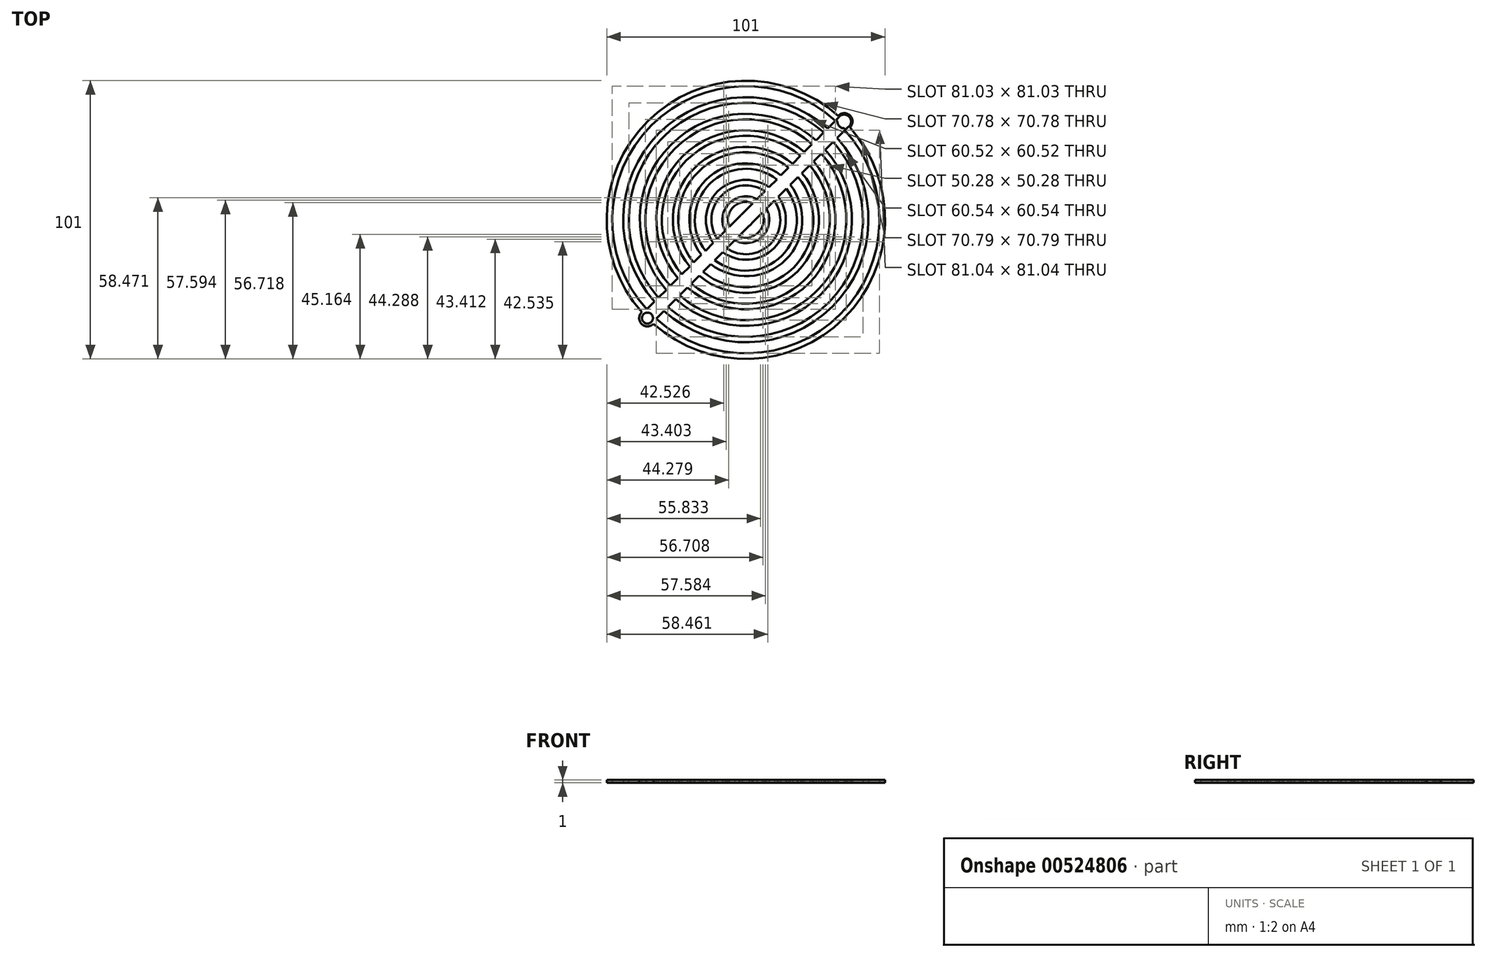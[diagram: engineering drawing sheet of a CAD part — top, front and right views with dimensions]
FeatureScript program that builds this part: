
annotation { "Feature Type Name" : "Feature", "Feature Type Description" : "" }
export const myFeature = defineFeature(function(context is Context, id is Id, definition is map)
    precondition{}
    {
        {
            var Q0;
            Q0=qCreatedBy(makeId("Top.planeOp"),FACE);
            var sketch = newSketch(context, id + "F0", { "sketchPlane" : qUnion([Q0])});
            skArc(sketch, "E0", {"start": v(-58.86, 36.16) * mm, "mid": v(-58.29, 36.6) * mm, "end": v(-57.86, 37.16) * mm});
            skArc(sketch, "E1.0", {"start": v(-57.5, 44.34) * mm, "mid": v(-64.65, 42.96) * mm, "end": v(-66.03, 35.8) * mm});
            skArc(sketch, "E2.0", {"start": v(-56, 45.83) * mm, "mid": v(-66.06, 44.37) * mm, "end": v(-67.52, 34.3) * mm});
            skArc(sketch, "E3.0", {"start": v(-53.1, 48.74) * mm, "mid": v(-68.9, 47.2) * mm, "end": v(-70.43, 31.4) * mm});
            skArc(sketch, "E4.0", {"start": v(-51.65, 50.18) * mm, "mid": v(-70.3, 48.61) * mm, "end": v(-71.87, 29.96) * mm});
            skLineSegment(sketch, "E5.bottom", {"start": v(-94.5, 72.8) * mm, "end": v(-25.6, 72.8) * mm, "construction": true});
            skLineSegment(sketch, "E5.top", {"start": v(-94.5, 3.92) * mm, "end": v(-25.6, 3.92) * mm, "construction": true});
            skLineSegment(sketch, "E5.left", {"start": v(-94.5, 72.8) * mm, "end": v(-94.5, 3.92) * mm, "construction": true});
            skLineSegment(sketch, "E5.right", {"start": v(-25.6, 72.8) * mm, "end": v(-25.6, 3.92) * mm, "construction": true});
            skArc(sketch, "E6.0", {"start": v(-48.8, 53.04) * mm, "mid": v(-73.13, 51.44) * mm, "end": v(-74.73, 27.1) * mm});
            skArc(sketch, "E7.0", {"start": v(-47.37, 54.46) * mm, "mid": v(-74.55, 52.86) * mm, "end": v(-76.16, 25.67) * mm});
            skArc(sketch, "E8.0", {"start": v(-44.52, 57.3) * mm, "mid": v(-77.38, 55.68) * mm, "end": v(-79, 22.83) * mm});
            skArc(sketch, "E9.0", {"start": v(-43.1, 58.73) * mm, "mid": v(-78.8, 57.1) * mm, "end": v(-80.42, 21.4) * mm});
            skArc(sketch, "E10.0", {"start": v(-40.26, 61.57) * mm, "mid": v(-81.62, 59.93) * mm, "end": v(-83.26, 18.57) * mm});
            skArc(sketch, "E11.0", {"start": v(-38.85, 62.99) * mm, "mid": v(-83.03, 61.34) * mm, "end": v(-84.68, 17.15) * mm});
            skArc(sketch, "E12.0", {"start": v(-36, 65.82) * mm, "mid": v(-85.86, 64.17) * mm, "end": v(-87.52, 14.32) * mm});
            skArc(sketch, "E13.0", {"start": v(-34.6, 67.24) * mm, "mid": v(-87.28, 65.58) * mm, "end": v(-88.93, 12.9) * mm});
            skArc(sketch, "E14.0", {"start": v(-31.76, 70.07) * mm, "mid": v(-90.1, 68.41) * mm, "end": v(-91.77, 10.07) * mm});
            skArc(sketch, "E15.0", {"start": v(-30.34, 71.49) * mm, "mid": v(-91.52, 69.83) * mm, "end": v(-93.18, 8.65) * mm});
            skArc(sketch, "E16.0", {"start": v(-27.51, 74.32) * mm, "mid": v(-94.35, 72.65) * mm, "end": v(-96.01, 5.82) * mm});
            skArc(sketch, "E17.0", {"start": v(-26.1, 75.74) * mm, "mid": v(-95.76, 74.07) * mm, "end": v(-97.43, 4.4) * mm});
            skLineSegment(sketch, "E18.0", {"start": v(-26.1, 75.74) * mm, "end": v(-27.3, 74.52) * mm});
            skLineSegment(sketch, "E19.0", {"start": v(-22.69, 72.33) * mm, "end": v(-23.92, 71.1) * mm});
            skLineSegment(sketch, "E20.trimOffspring", {"start": v(-48.8, 53.04) * mm, "end": v(-51.65, 50.18) * mm});
            skLineSegment(sketch, "E21.trimOffspring", {"start": v(-45.39, 49.64) * mm, "end": v(-48.25, 46.78) * mm});
            skLineSegment(sketch, "E22.trimOffspring", {"start": v(-44.52, 57.3) * mm, "end": v(-47.37, 54.46) * mm});
            skLineSegment(sketch, "E23", {"start": v(-96.22, 5.62) * mm, "end": v(-92.8, 2.23) * mm});
            skLineSegment(sketch, "E24", {"start": v(-27.3, 74.52) * mm, "end": v(-23.92, 71.1) * mm});
            skLineSegment(sketch, "E25.trimOffspring", {"start": v(-41.12, 53.9) * mm, "end": v(-43.96, 51.06) * mm});
            skLineSegment(sketch, "E26.trimOffspring", {"start": v(-36.86, 58.16) * mm, "end": v(-39.7, 55.33) * mm});
            skLineSegment(sketch, "E27.trimOffspring", {"start": v(-40.26, 61.57) * mm, "end": v(-43.1, 58.73) * mm});
            skLineSegment(sketch, "E28.trimOffspring", {"start": v(-36, 65.82) * mm, "end": v(-38.85, 62.99) * mm});
            skLineSegment(sketch, "E29.trimOffspring", {"start": v(-32.6, 62.42) * mm, "end": v(-35.44, 59.58) * mm});
            skLineSegment(sketch, "E30.trimOffspring", {"start": v(-28.35, 66.67) * mm, "end": v(-31.19, 63.83) * mm});
            skLineSegment(sketch, "E31.trimOffspring", {"start": v(-31.76, 70.07) * mm, "end": v(-34.6, 67.24) * mm});
            skLineSegment(sketch, "E32.trimOffspring", {"start": v(-27.51, 74.32) * mm, "end": v(-30.34, 71.49) * mm});
            skLineSegment(sketch, "E33.trimOffspring", {"start": v(-24.1, 70.92) * mm, "end": v(-26.94, 68.08) * mm});
            skLineSegment(sketch, "E34.trimOffspring", {"start": v(-53.1, 48.74) * mm, "end": v(-56, 45.83) * mm});
            skLineSegment(sketch, "E35.trimOffspring", {"start": v(-49.68, 45.34) * mm, "end": v(-52.6, 42.43) * mm});
            skLineSegment(sketch, "E36.trimOffspring", {"start": v(-57.5, 44.34) * mm, "end": v(-61.31, 40.52) * mm});
            skLineSegment(sketch, "E37.trimOffspring", {"start": v(-54.09, 40.94) * mm, "end": v(-57.86, 37.16) * mm});
            skArc(sketch, "E38.trimOffspring", {"start": v(-62.63, 32.4) * mm, "mid": v(-55.46, 33.76) * mm, "end": v(-54.09, 40.94) * mm});
            skLineSegment(sketch, "E39.trimOffspring", {"start": v(-62.21, 39.62) * mm, "end": v(-66.03, 35.8) * mm});
            skLineSegment(sketch, "E40.trimOffspring", {"start": v(-58.86, 36.16) * mm, "end": v(-62.63, 32.4) * mm});
            skArc(sketch, "E41.trimOffspring", {"start": v(-61.31, 40.52) * mm, "mid": v(-61.82, 40.13) * mm, "end": v(-62.21, 39.62) * mm});
            skArc(sketch, "E42.trimOffspring", {"start": v(-67.03, 27.99) * mm, "mid": v(-51.21, 29.52) * mm, "end": v(-49.68, 45.34) * mm});
            skArc(sketch, "E43.trimOffspring", {"start": v(-68.47, 26.55) * mm, "mid": v(-49.8, 28.1) * mm, "end": v(-48.25, 46.78) * mm});
            skLineSegment(sketch, "E44.trimOffspring", {"start": v(-67.52, 34.3) * mm, "end": v(-70.43, 31.4) * mm});
            skLineSegment(sketch, "E45.trimOffspring", {"start": v(-64.12, 30.9) * mm, "end": v(-67.03, 27.99) * mm});
            skLineSegment(sketch, "E46.trimOffspring", {"start": v(-68.47, 26.55) * mm, "end": v(-71.33, 23.7) * mm});
            skLineSegment(sketch, "E47.trimOffspring", {"start": v(-71.87, 29.96) * mm, "end": v(-74.73, 27.1) * mm});
            skLineSegment(sketch, "E48.trimOffspring", {"start": v(-76.16, 25.67) * mm, "end": v(-79, 22.83) * mm});
            skLineSegment(sketch, "E49.trimOffspring", {"start": v(-72.75, 22.27) * mm, "end": v(-75.6, 19.42) * mm});
            skLineSegment(sketch, "E50.trimOffspring", {"start": v(-77.02, 18) * mm, "end": v(-79.86, 15.16) * mm});
            skLineSegment(sketch, "E51.trimOffspring", {"start": v(-80.42, 21.4) * mm, "end": v(-83.26, 18.57) * mm});
            skArc(sketch, "E52.trimOffspring", {"start": v(-94.03, 1) * mm, "mid": v(-24.34, 2.65) * mm, "end": v(-22.69, 72.33) * mm});
            skLineSegment(sketch, "E53.trimOffspring", {"start": v(-96.22, 5.62) * mm, "end": v(-97.43, 4.4) * mm});
            skArc(sketch, "E54.trimOffspring", {"start": v(-92.61, 2.41) * mm, "mid": v(-25.76, 4.06) * mm, "end": v(-24.1, 70.92) * mm});
            skLineSegment(sketch, "E55.trimOffspring", {"start": v(-92.8, 2.23) * mm, "end": v(-94.03, 1) * mm});
            skArc(sketch, "E56.trimOffspring", {"start": v(-89.78, 5.24) * mm, "mid": v(-28.59, 6.9) * mm, "end": v(-26.94, 68.08) * mm});
            skLineSegment(sketch, "E57.trimOffspring", {"start": v(-89.78, 5.24) * mm, "end": v(-92.61, 2.41) * mm});
            skLineSegment(sketch, "E58.trimOffspring", {"start": v(-93.18, 8.65) * mm, "end": v(-96.01, 5.82) * mm});
            skArc(sketch, "E59.trimOffspring", {"start": v(-88.36, 6.66) * mm, "mid": v(-30, 8.3) * mm, "end": v(-28.35, 66.67) * mm});
            skArc(sketch, "E60.trimOffspring", {"start": v(-85.53, 9.5) * mm, "mid": v(-32.83, 11.14) * mm, "end": v(-31.19, 63.83) * mm});
            skLineSegment(sketch, "E61.trimOffspring", {"start": v(-88.93, 12.9) * mm, "end": v(-91.77, 10.07) * mm});
            skLineSegment(sketch, "E62.trimOffspring", {"start": v(-85.53, 9.5) * mm, "end": v(-88.36, 6.66) * mm});
            skArc(sketch, "E63.trimOffspring", {"start": v(-84.11, 10.91) * mm, "mid": v(-34.24, 12.55) * mm, "end": v(-32.6, 62.42) * mm});
            skArc(sketch, "E64.trimOffspring", {"start": v(-81.28, 13.75) * mm, "mid": v(-37.07, 15.38) * mm, "end": v(-35.44, 59.58) * mm});
            skLineSegment(sketch, "E65.trimOffspring", {"start": v(-84.68, 17.15) * mm, "end": v(-87.52, 14.32) * mm});
            skLineSegment(sketch, "E66.trimOffspring", {"start": v(-81.28, 13.75) * mm, "end": v(-84.11, 10.91) * mm});
            skArc(sketch, "E67.trimOffspring", {"start": v(-79.86, 15.16) * mm, "mid": v(-38.49, 16.8) * mm, "end": v(-36.86, 58.16) * mm});
            skArc(sketch, "E68.trimOffspring", {"start": v(-77.02, 18) * mm, "mid": v(-41.31, 19.62) * mm, "end": v(-39.7, 55.33) * mm});
            skArc(sketch, "E69.trimOffspring", {"start": v(-75.6, 19.42) * mm, "mid": v(-42.73, 21.04) * mm, "end": v(-41.12, 53.9) * mm});
            skArc(sketch, "E70.trimOffspring", {"start": v(-72.75, 22.27) * mm, "mid": v(-45.56, 23.86) * mm, "end": v(-43.96, 51.06) * mm});
            skArc(sketch, "E71.trimOffspring", {"start": v(-71.33, 23.7) * mm, "mid": v(-46.97, 25.28) * mm, "end": v(-45.39, 49.64) * mm});
            skArc(sketch, "E72.trimOffspring", {"start": v(-64.12, 30.9) * mm, "mid": v(-54.04, 32.35) * mm, "end": v(-52.6, 42.43) * mm});
            skArc(sketch, "E73", {"start": v(-23.92, 71.1) * mm, "mid": v(-22.21, 76.18) * mm, "end": v(-27.3, 74.52) * mm});
            skCircle(sketch, "E74", {"center": v(-24.34, 74.07) * mm, "radius": 2.5 * mm});
            skArc(sketch, "E75", {"start": v(-96.22, 5.62) * mm, "mid": v(-97.87, 0.52) * mm, "end": v(-92.8, 2.23) * mm});
            skCircle(sketch, "E76", {"center": v(-95.76, 2.65) * mm, "radius": 2 * mm});
            skLineSegment(sketch, "E77", {"start": v(-24.34, 74.07) * mm, "end": v(-95.76, 2.65) * mm, "construction": true});
            skSolve(sketch);
        }
        {
            var Q0;
            Q0 = qSketchRegion(id + "F0", true);
            var Q1;
            Q1=makeQuery(id+"F0.imprint","IMPRINT",FACE,{"disambiguationData":[TD([[makeQuery(id+"F0.imprint","IMPRINT",EDGE,{"derivedFrom":sQuery(id+"F0.wireOp",EDGE,"E1.0")}),-1.0]])]});
            var Q2;
            Q2=makeQuery(id+"F0.imprint","IMPRINT",FACE,{"disambiguationData":[TD([[makeQuery(id+"F0.imprint","IMPRINT",EDGE,{"derivedFrom":sQuery(id+"F0.wireOp",EDGE,"E0")}),1.0]])]});
            extrude(context, id + "F1", {"entities" : qUnion([Q0, Q1, Q2]), "depth" : 1 * mm, "offsetDistance" : 25 * mm});
        }
    });
